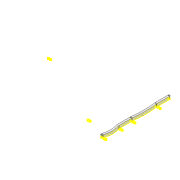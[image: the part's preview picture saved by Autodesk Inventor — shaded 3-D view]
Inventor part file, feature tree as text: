
AUTODESK INVENTOR PART (.ipt)
format: ipt  version: 2022 (Build 260153000, 153)  size: 151,040 bytes
history: native  units: mm
features: sketch x2, extrude x1, other x1, fillet x1, projected_geometry x1
ambient origin geometry x8: Origin, YZ Plane, XZ Plane, XY Plane, X Axis, Y Axis, Z Axis, Center Point
bodies: Solid1 (feature_tree)
feature tree (6):
  extrude  "Extrusion1"  Depth=6.0mm
  other  "Work Axis1"
  fillet  "Fillet1"  Radius=3.0mm
  sketch  "Sketch2"  dims[d3=3.0mm d4=8.0mm d5=0.0mm d6=3.0mm d7=171.332mm d8=3.0mm d9=92.628mm d10=300.0mm d11=300.0mm d14=2.0mm d15=50.0mm d16=70.0mm d17=70.0mm d18=10.0mm]
  sketch  "Sketch1"  dims[d0=212.9mm d1=6.0mm d2=3.0mm]
  projected_geometry  "Projected Loop1"
